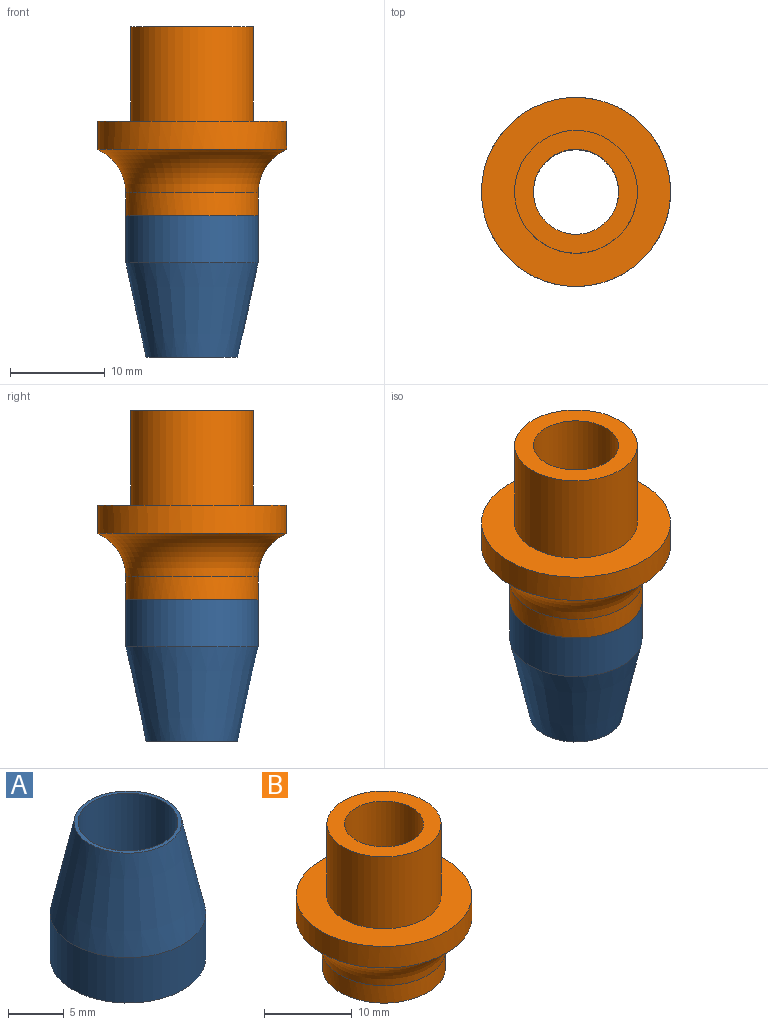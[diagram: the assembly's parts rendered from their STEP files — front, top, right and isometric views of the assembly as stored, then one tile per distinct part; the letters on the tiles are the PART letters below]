
ASSEMBLY  parts=2 mates=1
PART A: 5 faces, bbox 14x14x15 mm
  f0: plane 9.7x9.7mm, normal (0,0,1), area 10.3mm2, adj f1,f4
  f1: cone r=4.85mm half-angle=12.1deg, axis (0,0,-1), area 380.8mm2, adj f0,f2
  f2: cylinder r=7mm len=14mm, axis (0,0,1), area 219.9mm2, adj f1,f3
  f3: plane 14x14mm, normal (0,0,-1), area 90.3mm2, adj f2,f4
  f4: cylinder r=4.5mm len=15mm, axis (0,0,-1), area 424.1mm2, adj f0,f3
PART B: 8 faces, bbox 26x26x21.1 mm
  f0: cylinder r=4.5mm len=20mm, axis (0,0,-1), area 565.5mm2, adj f2,f6
  f1: cylinder r=6.5mm len=13mm, axis (0,0,-1), area 408.4mm2, adj f2,f4
  f2: plane 13x13mm, normal (0,0,1), area 69.1mm2, adj f0,f1
  f3: cylinder r=10mm len=20mm, axis (0,0,1), area 188.5mm2, adj f4,f7
  f4: plane 20x20mm, normal (0,0,1), area 181.4mm2, adj f1,f3
  f5: cylinder r=7mm len=14mm, axis (0,0,1), area 106.3mm2, adj f6,f7
  f6: plane 14x14mm, normal (0,0,-1), area 90.3mm2, adj f0,f5
  f7: torus R=12mm, axis (0,0,1), area 293.1mm2, adj f3,f5
PLACE A rot(axis=(1,0,0),180deg) t=(12.64,5.44,-24.38)mm
PLACE B t=(12.64,5.44,-9.38)mm
MATE fastened B.f3 <-> A.f1  axis (0,0,-1) through (12.64,5.44,-19.38)mm
